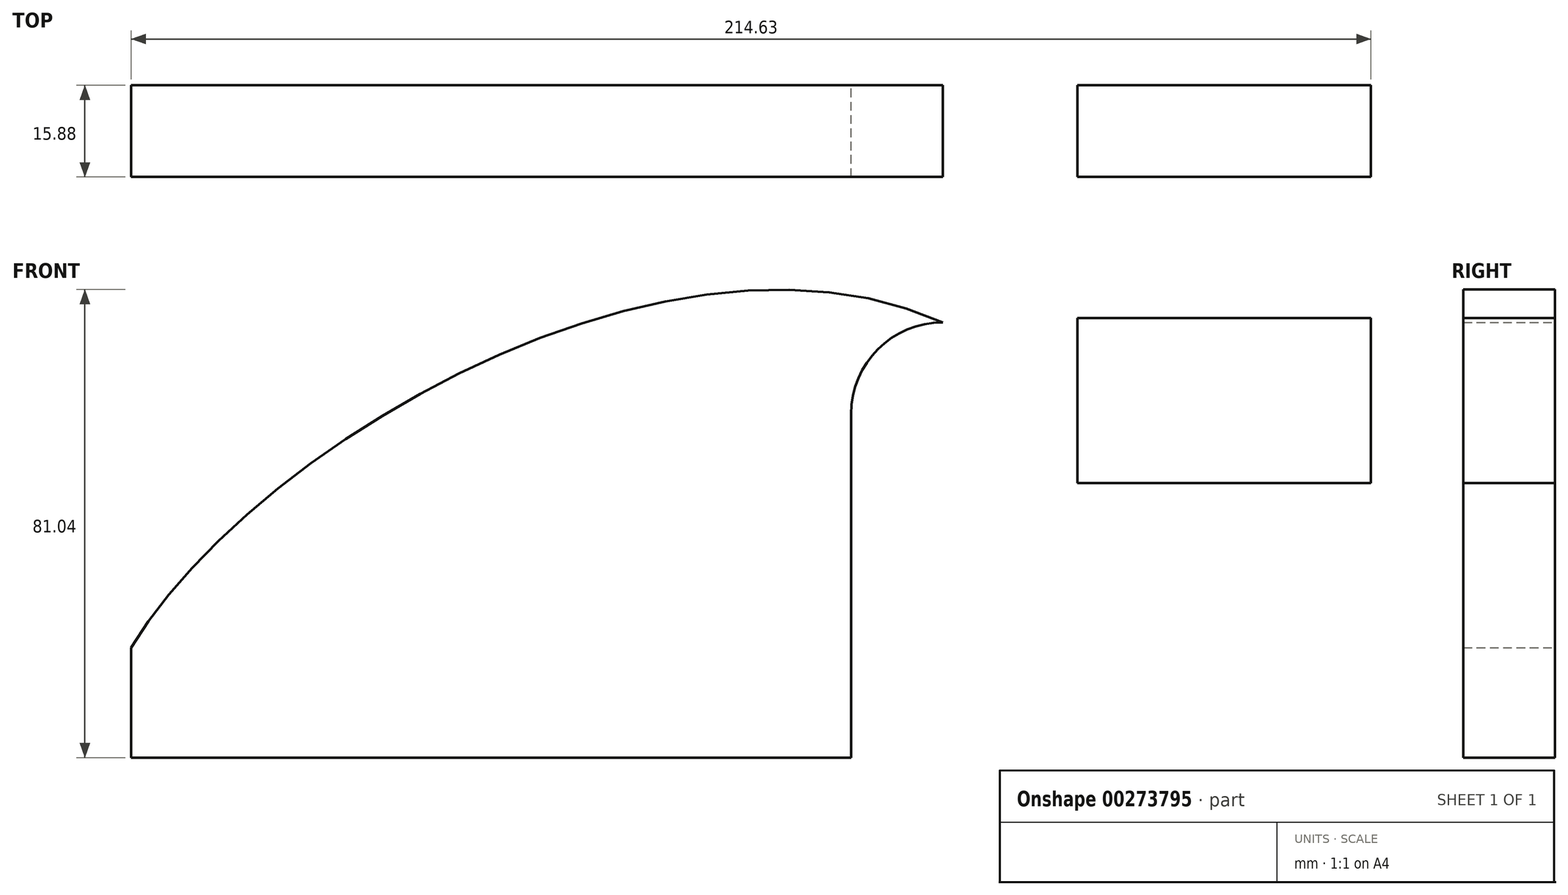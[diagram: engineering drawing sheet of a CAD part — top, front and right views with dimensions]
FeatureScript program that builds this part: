
annotation { "Feature Type Name" : "Feature", "Feature Type Description" : "" }
export const myFeature = defineFeature(function(context is Context, id is Id, definition is map)
    precondition{}
    {
        {
            var Q0;
            Q0=qCreatedBy(makeId("Front.planeOp"),FACE);
            var sketch = newSketch(context, id + "F0", { "sketchPlane" : qUnion([Q0])});
            skLineSegment(sketch, "E0.bottom", {"start": v(-62.32, -9.53) * mm, "end": v(62.32, -9.53) * mm});
            skLineSegment(sketch, "E0.top", {"start": v(-62.32, 9.52) * mm, "end": v(62.32, 9.52) * mm});
            skLineSegment(sketch, "E0.left", {"start": v(-62.32, -9.53) * mm, "end": v(-62.32, 9.52) * mm});
            skLineSegment(sketch, "E0.right", {"start": v(62.32, -9.53) * mm, "end": v(62.32, 9.52) * mm});
            skPoint(sketch, "E0.middle", {"position": v(0, 0) * mm});
            skLineSegment(sketch, "E1.bottom", {"start": v(101.51, 38) * mm, "end": v(152.31, 38) * mm});
            skLineSegment(sketch, "E1.top", {"start": v(101.51, 66.58) * mm, "end": v(152.31, 66.58) * mm});
            skLineSegment(sketch, "E1.left", {"start": v(101.51, 38) * mm, "end": v(101.51, 66.58) * mm});
            skLineSegment(sketch, "E1.right", {"start": v(152.31, 38) * mm, "end": v(152.31, 66.58) * mm});
            skPoint(sketch, "E1.middle", {"position": v(126.91, 52.3) * mm});
            skLineSegment(sketch, "E2", {"start": v(62.32, 9.52) * mm, "end": v(62.32, 49.97) * mm});
            skArc(sketch, "E3", {"start": v(62.32, 49.97) * mm, "mid": v(66.97, 61.2) * mm, "end": v(78.2, 65.84) * mm});
            skLineSegment(sketch, "E4", {"start": v(78.2, 65.84) * mm, "end": v(130.6, 65.84) * mm});
            skFitSpline(sketch, "E5", {"points": [v(-62.32, 9.52) * mm, v(78.2, 65.84) * mm], "startDerivative": vector(62.32, 103.86) * mm, "endDerivative": vector(142.53, -63.81) * mm});
            skSolve(sketch);
        }
        {
            var Q0;
            Q0=makeQuery(id+"F0.imprint","IMPRINT",FACE,{"disambiguationData":[TD([[makeQuery(id+"F0.imprint","IMPRINT",EDGE,{"derivedFrom":sQuery(id+"F0.wireOp",EDGE,"E0.bottom")}),1.0]])]});
            var Q1;
            Q1=makeQuery(id+"F0.imprint","IMPRINT",FACE,{"disambiguationData":[TD([[makeQuery(id+"F0.imprint","IMPRINT",EDGE,{"derivedFrom":sQuery(id+"F0.wireOp",EDGE,"E0.top")}),1.0]])]});
            var Q2;
            {var subQ0=sQuery(id+"F0.wireOp",EDGE,"E1.bottom");Q2=makeQuery(id+"F0.imprint","IMPRINT",FACE,{"disambiguationData":[TD([[makeQuery(id+"F0.imprint","IMPRINT",EDGE,{"derivedFrom":subQ0}),1.0]])]});}
            extrude(context, id + "F1", {"entities" : qUnion([Q0, Q1, Q2]), "endBound" : BoundingType.SYMMETRIC, "depth" : 15.88 * mm});
        }
    });
